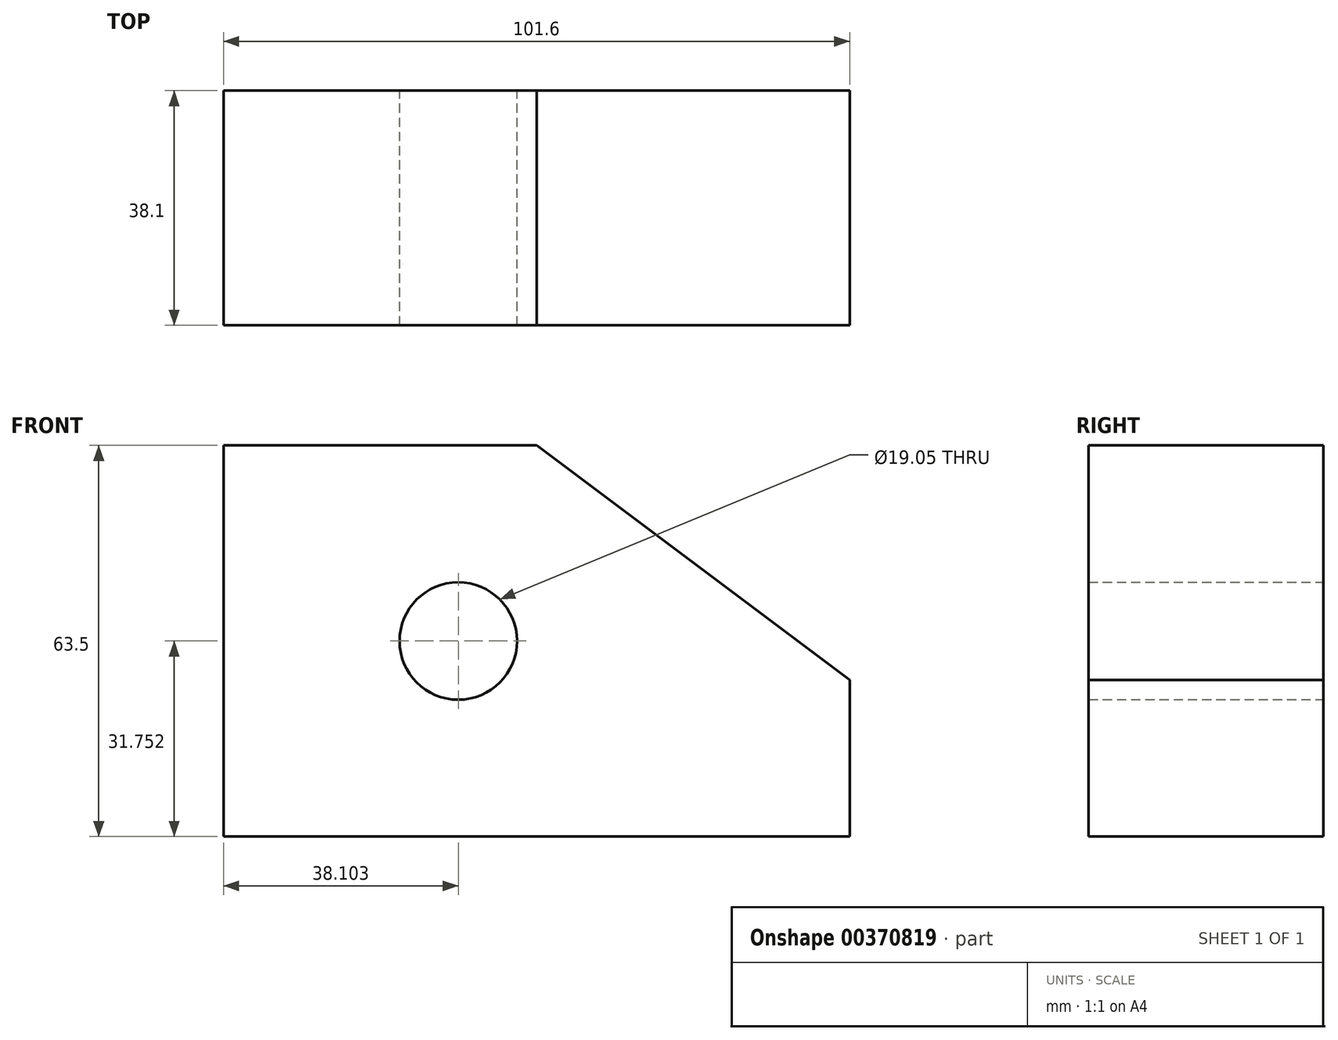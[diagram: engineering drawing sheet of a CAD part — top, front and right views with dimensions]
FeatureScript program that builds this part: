
annotation { "Feature Type Name" : "Feature", "Feature Type Description" : "" }
export const myFeature = defineFeature(function(context is Context, id is Id, definition is map)
    precondition{}
    {
        {
            var Q0;
            Q0=qCreatedBy(makeId("Front.planeOp"),FACE);
            var sketch = newSketch(context, id + "F0", { "sketchPlane" : qUnion([Q0])});
            skLineSegment(sketch, "E0", {"start": v(-58.59, 13.51) * mm, "end": v(-58.59, -49.99) * mm});
            skLineSegment(sketch, "E1", {"start": v(-58.59, -49.99) * mm, "end": v(43.01, -49.99) * mm});
            skLineSegment(sketch, "E2", {"start": v(43.01, -49.99) * mm, "end": v(43.01, -24.59) * mm});
            skLineSegment(sketch, "E3", {"start": v(-58.59, 13.51) * mm, "end": v(-7.79, 13.51) * mm});
            skLineSegment(sketch, "E4", {"start": v(-7.79, 13.51) * mm, "end": v(43.01, -24.59) * mm});
            skCircle(sketch, "E5", {"center": v(-20.49, -18.24) * mm, "radius": 9.53 * mm});
            skSolve(sketch);
        }
        {
            var Q0;
            Q0=makeQuery(id+"F0.imprint","IMPRINT",FACE,{"disambiguationData":[TD([[makeQuery(id+"F0.imprint","IMPRINT",EDGE,{"derivedFrom":sQuery(id+"F0.wireOp",EDGE,"E0")}),1.0]])]});
            extrude(context, id + "F1", {"entities" : qUnion([Q0]), "depth" : 38.1 * mm});
        }
    });
